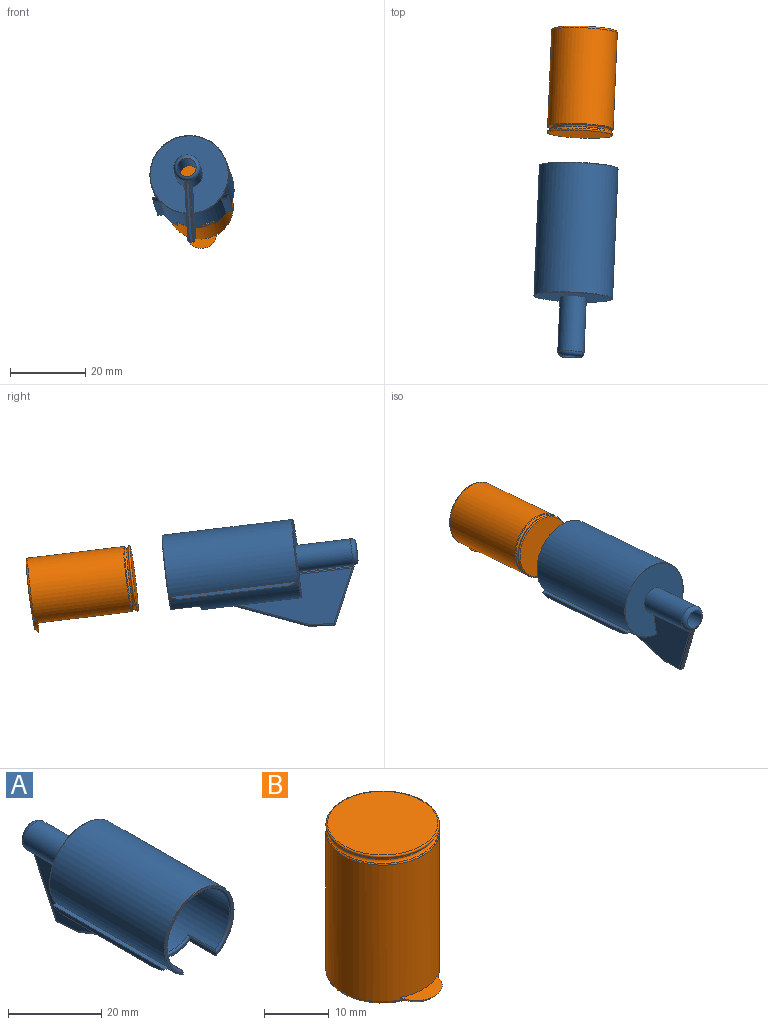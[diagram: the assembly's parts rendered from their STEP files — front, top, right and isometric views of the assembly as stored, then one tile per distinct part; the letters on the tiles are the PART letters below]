
ASSEMBLY  parts=2 mates=1
PART A: 81 faces, bbox 22.8x51x30.3 mm
  f0: cylinder r=9.5mm len=33.5mm, axis (0,1,0), area 1911.1mm2, adj f7,f28,f29,f30,f31
  f1: plane 20.8x20.77mm, normal (0,1,0), area 290.5mm2, adj f3,f8,f9,f10,f13,f14,f15,f16
  f2: cone r=0.52mm half-angle=59deg, axis (0,1,0), area 5.4mm2, adj f6,f7
  f3: cylinder r=3.5mm len=14.82mm, axis (0,1,0), area 325.8mm2, adj f1,f43
  f4: cylinder r=10.5mm len=34.8mm, axis (0,1,0), area 2108.6mm2, adj f8,f9,f11,f18,f21,f25,f26,f27
  f5: plane 20.8x19.52mm, normal (0,-1,0), area 21.5mm2, adj f25,f26,f30,f50
  f6: cylinder r=2.5mm len=17.17mm, axis (0,1,0), area 269.7mm2, adj f2,f43
  f7: plane 19x19mm, normal (0,-1,0), area 259.3mm2, adj f0,f2
  f8: plane 31.32x14.19mm, normal (1,0,0), area 211.1mm2, adj f1,f4,f15,f18,f19,f34,f51
  f9: plane 31.32x14.19mm, normal (-1,0,0), area 211.1mm2, adj f1,f4,f16,f20,f21,f40,f51
  f10: plane 14.37x0.6mm, normal (0,0,1), area 8.6mm2, adj f1,f13,f14,f37
  f11: plane 19.29x7.81mm, normal (0,-0.37,-0.93), area 12.5mm2, adj f4,f18,f21,f24
  f12: plane 6.41x0.6mm, normal (0,-0.09,-1), area 3.9mm2, adj f17,f19,f20,f24
  f13: plane 14.43x0.36mm, normal (-0.71,0,0.71), area 7.2mm2, adj f1,f10,f16,f37,f38
  f14: plane 14.43x0.36mm, normal (0.71,0,0.71), area 7.2mm2, adj f1,f10,f15,f36,f37
  f15: cylinder r=0.5mm len=14.26mm, axis (0,-1,0), area 5.6mm2, adj f1,f8,f14,f35
  f16: cylinder r=0.5mm len=14.26mm, axis (0,1,0), area 5.6mm2, adj f1,f9,f13,f39
  f17: cylinder r=0.5mm len=0.77mm, axis (-1,0,0), area 0.3mm2, adj f12,f32,f42,f76
  f18: cylinder r=0.5mm len=19.46mm, axis (0,-0.93,0.37), area 15.9mm2, adj f4,f8,f11,f22
  f19: cylinder r=0.5mm len=6.56mm, axis (0,-1,0.09), area 5.1mm2, adj f8,f12,f22,f32,f33
  f20: cylinder r=0.5mm len=6.56mm, axis (0,1,-0.09), area 5.1mm2, adj f9,f12,f23,f41,f42
  f21: cylinder r=0.5mm len=19.46mm, axis (0,0.93,-0.37), area 15.9mm2, adj f4,f9,f11,f23
  f22: sphere r=0.5mm, area 0.1mm2, adj f18,f19,f24
  f23: sphere r=0.5mm, area 0.1mm2, adj f20,f21,f24
  f24: cylinder r=0.5mm len=0.6mm, axis (1,0,0), area 0.1mm2, adj f11,f12,f22,f23
  f25: plane 8.1x0.9mm, normal (-1,0,0), area 7mm2, adj f4,f5,f27,f29,f30,f31,f50
  f26: plane 8.1x0.9mm, normal (1,0,0), area 7mm2, adj f4,f5,f27,f28,f29,f30,f50
  f27: plane 10x1.84mm, normal (0,-1,0), area 5.2mm2, adj f4,f25,f26,f29
  f28: cylinder r=0.5mm len=8.42mm, axis (0,1,0), area 4mm2, adj f0,f26,f29,f30
  f29: torus R=10mm, axis (0,-1,0), area 8.4mm2, adj f0,f25,f26,f27,f28,f31
  f30: torus R=10mm, axis (0,-1,0), area 39.4mm2, adj f0,f5,f25,f26,f28,f31
  f31: cylinder r=0.5mm len=8.42mm, axis (0,1,0), area 4mm2, adj f0,f25,f29,f30
  f32: bspline ~0.51x0.48mm, area 0.2mm2, adj f17,f19,f33,f72,f74
  f33: bspline ~0.46x0.44mm, area 0.1mm2, adj f19,f32,f34,f70
  f34: cylinder r=0.4mm len=14.34mm, axis (0,-0.42,-0.91), area 7.7mm2, adj f8,f33,f35,f68
  f35: bspline ~0.74x0.61mm, area 0.2mm2, adj f15,f34,f36,f67
  f36: cylinder r=0.4mm len=0.71mm, axis (0.67,-0.31,-0.67), area 0.3mm2, adj f14,f35,f37,f69
  f37: cylinder r=0.4mm len=0.62mm, axis (1,0,0), area 0.4mm2, adj f10,f13,f14,f36,f38,f71
  f38: cylinder r=0.4mm len=0.71mm, axis (-0.67,-0.31,-0.67), area 0.3mm2, adj f13,f37,f39,f73
  f39: bspline ~0.74x0.61mm, area 0.2mm2, adj f16,f38,f40,f75
  f40: cylinder r=0.4mm len=14.34mm, axis (0,0.42,0.91), area 7.7mm2, adj f9,f39,f41,f77
  f41: bspline ~0.46x0.44mm, area 0.1mm2, adj f20,f40,f42,f79
  f42: bspline ~0.51x0.48mm, area 0.2mm2, adj f17,f20,f41,f78,f80
  f43: torus R=2.3mm, axis (0,1,0), area 33.3mm2, adj f3,f6
  f44: plane 34x1mm, normal (-1,0,0), area 32.1mm2, adj f45,f46,f52,f53
  f45: plane 28x1.84mm, normal (0,0,-1), area 51.6mm2, adj f4,f44,f52,f53
  f46: plane 34x1.13mm, normal (0,0,1), area 38.3mm2, adj f4,f44,f52,f53
  f47: plane 34x1.13mm, normal (0,0,1), area 38.3mm2, adj f4,f49,f54,f55
  f48: plane 28x1.84mm, normal (0,0,-1), area 51.6mm2, adj f4,f49,f54,f55
  f49: plane 34x1mm, normal (1,0,0), area 32.1mm2, adj f47,f48,f54,f55
  f50: torus R=10.4mm, axis (0,-1,0), area 8.7mm2, adj f4,f5,f25,f26
  f51: torus R=10.4mm, axis (0,-1,0), area 10.1mm2, adj f1,f4,f8,f9
  f52: cylinder r=5mm len=3mm, axis (-1,0,0), area 4.8mm2, adj f4,f44,f45,f46
  f53: cylinder r=5mm len=3mm, axis (-1,0,0), area 4.8mm2, adj f4,f44,f45,f46
  f54: cylinder r=5mm len=3mm, axis (-1,0,0), area 4.8mm2, adj f4,f47,f48,f49
  f55: cylinder r=5mm len=3mm, axis (-1,0,0), area 4.8mm2, adj f4,f47,f48,f49
  f56: plane 14.25x6.79mm, normal (1,0,0), area 2.9mm2, adj f57,f65,f66,f77
  f57: extruded ~0.2x0.15mm, area 0mm2, adj f56,f58,f66,f75
  f58: plane 0.31x0.28mm, normal (0.74,-0.28,-0.61), area 0.1mm2, adj f57,f59,f66,f73
  f59: plane 0.27x0.17mm, normal (0,-0.42,-0.91), area 0mm2, adj f58,f60,f66,f71
  f60: plane 0.31x0.28mm, normal (-0.74,-0.28,-0.61), area 0.1mm2, adj f59,f61,f66,f69
  f61: extruded ~0.2x0.15mm, area 0mm2, adj f60,f62,f66,f67
  f62: plane 14.25x6.79mm, normal (-1,0,0), area 2.9mm2, adj f61,f63,f66,f68
  f63: extruded ~0.18x0.11mm, area 0mm2, adj f62,f64,f66,f70
  f64: plane 0.79x0.17mm, normal (0,0.42,0.91), area 0.1mm2, adj f63,f65,f66,f70,f74,f76,f78,f79
  f65: extruded ~0.18x0.11mm, area 0mm2, adj f56,f64,f66,f79
  f66: plane 14.52x6.78mm, normal (0,0.91,-0.42), area 12.7mm2, adj f56,f57,f58,f59,f60,f61,f62,f63
  f67: bspline ~0.23x0.18mm, area 0mm2, adj f35,f61,f68,f69
  f68: cylinder r=0.1mm len=14.22mm, axis (0,-0.42,-0.91), area 3mm2, adj f34,f62,f67,f70
  f69: cylinder r=0.1mm len=0.38mm, axis (0.67,-0.31,-0.67), area 0.1mm2, adj f36,f60,f67,f71
  f70: bspline ~0.15x0.14mm, area 0mm2, adj f33,f63,f64,f68,f72,f74
  f71: cylinder r=0.1mm len=0.39mm, axis (1,0,0), area 0.1mm2, adj f37,f59,f69,f73
  f72: bspline ~0.2x0.18mm, area 0mm2, adj f32,f70,f74
  f73: cylinder r=0.1mm len=0.38mm, axis (-0.67,-0.31,-0.67), area 0.1mm2, adj f38,f58,f71,f75
  f74: bspline ~0.25x0.16mm, area 0mm2, adj f32,f64,f70,f72,f76
  f75: bspline ~0.23x0.18mm, area 0mm2, adj f39,f57,f73,f77
  f76: cylinder r=0.1mm len=0.77mm, axis (-1,0,0), area 0.1mm2, adj f17,f64,f74,f78
  f77: cylinder r=0.1mm len=14.22mm, axis (0,0.42,0.91), area 3mm2, adj f40,f56,f75,f79
  f78: bspline ~0.25x0.16mm, area 0mm2, adj f42,f64,f76,f79,f80
  f79: bspline ~0.15x0.14mm, area 0mm2, adj f41,f64,f65,f77,f78,f80
  f80: bspline ~0.2x0.18mm, area 0mm2, adj f42,f78,f79
PART B: 15 faces, bbox 19.1x20.8x28 mm
  f0: cylinder r=8.75mm len=25.75mm, axis (0,0,-1), area 1411.7mm2, adj f1,f6,f9,f10,f11
  f1: cylinder r=8.75mm len=0.55mm, axis (0,0,-1), area 0.2mm2, adj f0,f10,f11
  f2: plane 18.34x16.5mm, normal (0,0,-1), area 20.6mm2, adj f4,f11,f12
  f3: cone r=0mm half-angle=59deg, axis (0,0,-1), area 234.6mm2, adj f4
  f4: cylinder r=8mm len=21.5mm, axis (0,0,-1), area 1080.7mm2, adj f2,f3
  f5: cylinder r=8.25mm len=16.5mm, axis (0,0,-1), area 0.9mm2, adj f13,f14
  f6: plane 7.94x3.5mm, normal (0,0,1), area 16.1mm2, adj f0,f10
  f7: plane 17x17mm, normal (0,0,1), area 227mm2, adj f8
  f8: torus R=8.5mm, axis (0,0,1), area 37.6mm2, adj f7,f14
  f9: torus R=8.5mm, axis (0,0,1), area 16.2mm2, adj f0,f13
  f10: cone r=4mm half-angle=45deg, axis (0,0,1), area 11.9mm2, adj f0,f1,f6,f11,f12
  f11: torus R=8.25mm, axis (0,0,1), area 37.3mm2, adj f0,f1,f2,f10,f12
  f12: torus R=2.79mm, axis (0,0,1), area 3.2mm2, adj f2,f10,f11
  f13: torus R=8.8mm, axis (0,0,1), area 34.3mm2, adj f5,f9
  f14: torus R=8.8mm, axis (0,0,1), area 34.3mm2, adj f5,f8
PLACE A rot(axis=(-0.02,0.06,1),177.7deg) t=(-24.85,-175.64,61.4)mm
PLACE B rot(axis=(1,-0.04,0),83.1deg) t=(-21.21,-89.47,50.97)mm
MATE slider B.f8 <-> A.f0  axis (-0.04,-0.99,0.12) through (-22.38,-117.24,54.33)mm
